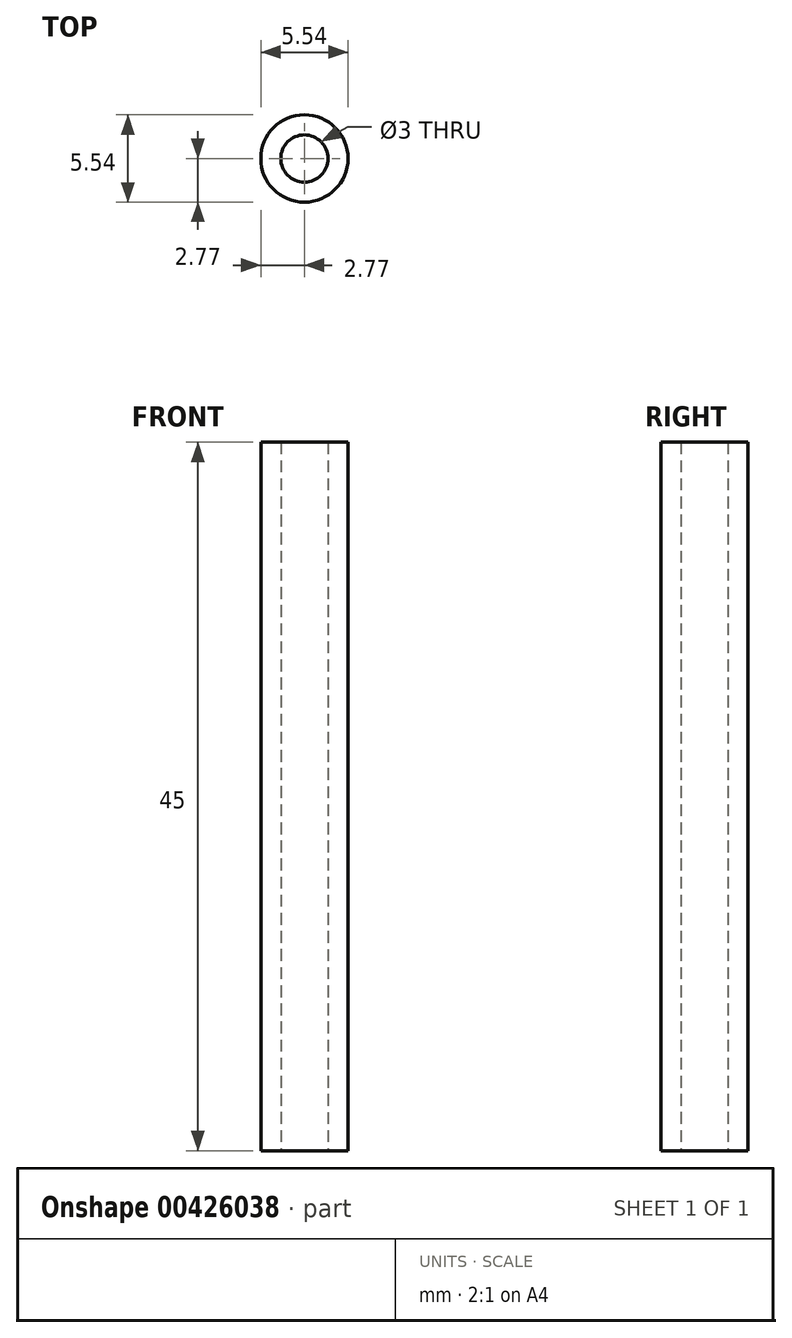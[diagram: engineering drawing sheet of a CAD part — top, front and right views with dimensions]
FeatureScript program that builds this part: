
annotation { "Feature Type Name" : "Feature", "Feature Type Description" : "" }
export const myFeature = defineFeature(function(context is Context, id is Id, definition is map)
    precondition{}
    {
        {
            var Q0;
            Q0=qCreatedBy(makeId("Top.planeOp"),FACE);
            var sketch = newSketch(context, id + "F0", { "sketchPlane" : qUnion([Q0])});
            skCircle(sketch, "E0", {"center": v(0, 0) * mm, "radius": 1.5 * mm});
            skCircle(sketch, "E1", {"center": v(0, 0) * mm, "radius": 2.77 * mm});
            skSolve(sketch);
        }
        {
            var Q0;
            Q0=makeQuery(id+"F0.imprint","IMPRINT",FACE,{"disambiguationData":[TD([[makeQuery(id+"F0.imprint","IMPRINT",EDGE,{"derivedFrom":sQuery(id+"F0.wireOp",EDGE,"E0")}),-1.0]])]});
            extrude(context, id + "F1", {"entities" : qUnion([Q0]), "depth" : 45 * mm});
        }
    });
